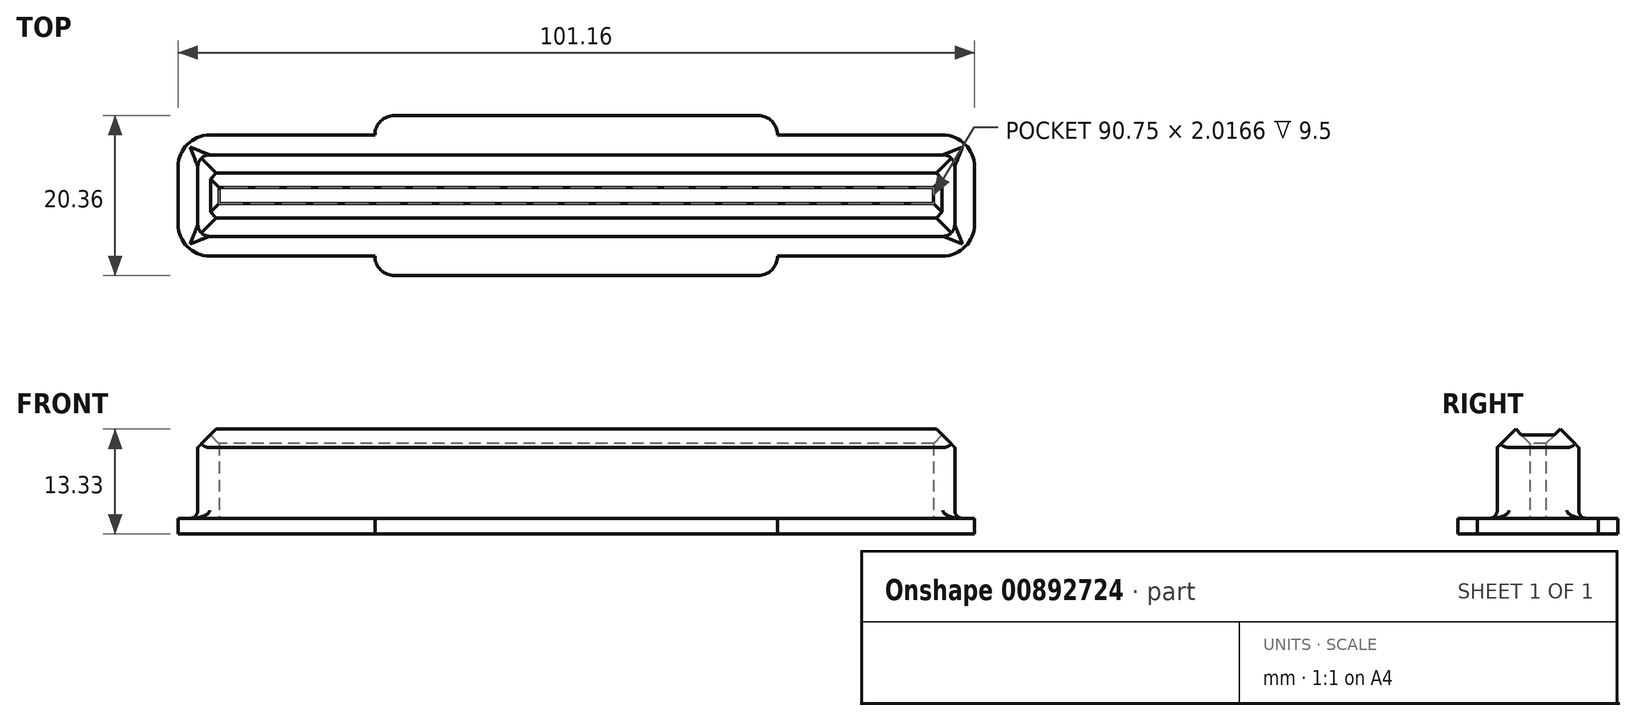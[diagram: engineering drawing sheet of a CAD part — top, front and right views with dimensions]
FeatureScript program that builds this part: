
annotation { "Feature Type Name" : "Feature", "Feature Type Description" : "" }
export const myFeature = defineFeature(function(context is Context, id is Id, definition is map)
    precondition{}
    {
        {
            var Q0;
            Q0=qCreatedBy(makeId("Top.planeOp"),FACE);
            var sketch = newSketch(context, id + "F0", { "sketchPlane" : qUnion([Q0])});
            skLineSegment(sketch, "E0.bottom", {"start": v(48.08, 5.18) * mm, "end": v(-48.08, 5.18) * mm});
            skLineSegment(sketch, "E0.top", {"start": v(48.08, -5.17) * mm, "end": v(-48.08, -5.17) * mm});
            skLineSegment(sketch, "E0.left", {"start": v(48.08, 5.17) * mm, "end": v(48.08, -5.18) * mm});
            skLineSegment(sketch, "E0.right", {"start": v(-48.08, 5.18) * mm, "end": v(-48.08, -5.17) * mm});
            skPoint(sketch, "E0.middle", {"position": v(0, 0) * mm});
            skLineSegment(sketch, "E1.bottom", {"start": v(-50.58, 7.68) * mm, "end": v(50.58, 7.68) * mm});
            skLineSegment(sketch, "E1.top", {"start": v(-50.58, -7.68) * mm, "end": v(50.58, -7.68) * mm});
            skLineSegment(sketch, "E1.left", {"start": v(-50.58, 7.68) * mm, "end": v(-50.58, -7.67) * mm});
            skLineSegment(sketch, "E1.right", {"start": v(50.58, 7.67) * mm, "end": v(50.58, -7.68) * mm});
            skLineSegment(sketch, "E2.bottom", {"start": v(-45.38, 1) * mm, "end": v(45.38, 1) * mm});
            skLineSegment(sketch, "E2.top", {"start": v(-45.38, -1) * mm, "end": v(45.38, -1) * mm});
            skLineSegment(sketch, "E2.left", {"start": v(-45.38, 1) * mm, "end": v(-45.38, -1) * mm});
            skLineSegment(sketch, "E2.right", {"start": v(45.38, 1) * mm, "end": v(45.38, -1) * mm});
            skLineSegment(sketch, "E3", {"start": v(-25.57, 7.67) * mm, "end": v(-25.57, 10.18) * mm});
            skLineSegment(sketch, "E4", {"start": v(-25.57, 10.18) * mm, "end": v(0, 10.18) * mm});
            skLineSegment(sketch, "E5.MirrorCS", {"start": v(25.57, 10.18) * mm, "end": v(0, 10.17) * mm});
            skLineSegment(sketch, "E6.MirrorCS", {"start": v(25.57, 7.67) * mm, "end": v(25.57, 10.18) * mm});
            skLineSegment(sketch, "E7.MirrorCS", {"start": v(-25.58, -7.67) * mm, "end": v(-25.58, -10.18) * mm});
            skLineSegment(sketch, "E8.MirrorCS", {"start": v(-25.57, -10.18) * mm, "end": v(0, -10.17) * mm});
            skLineSegment(sketch, "E9.MirrorCS", {"start": v(25.57, -10.18) * mm, "end": v(0, -10.18) * mm});
            skLineSegment(sketch, "E10.MirrorCS", {"start": v(25.57, -7.67) * mm, "end": v(25.57, -10.18) * mm});
            skSolve(sketch);
        }
        {
            var Q0;
            Q0=makeQuery(id+"F0.imprint","IMPRINT",FACE,{"disambiguationData":[TD([[makeQuery(id+"F0.imprint","IMPRINT",EDGE,{"derivedFrom":sQuery(id+"F0.wireOp",EDGE,"E0.bottom")}),-1.0]])]});
            var Q1;
            Q1=makeQuery(id+"F0.imprint","IMPRINT",FACE,{"disambiguationData":[TD([[makeQuery(id+"F0.imprint","IMPRINT",EDGE,{"derivedFrom":sQuery(id+"F0.wireOp",EDGE,"E0.bottom")}),1.0]])]});
            var Q2;
            Q2=makeQuery(id+"F0.imprint","IMPRINT",FACE,{"disambiguationData":[TD([[makeQuery(id+"F0.imprint","IMPRINT",EDGE,{"derivedFrom":sQuery(id+"F0.wireOp",EDGE,"E2.bottom")}),-1.0]])]});
            extrude(context, id + "F1", {"entities" : qUnion([Q0, Q1, Q2]), "oppositeDirection" : true, "depth" : 2 * mm, "offsetDistance" : 25 * mm});
        }
        {
            var Q0;
            Q0=makeQuery(id+"F0.imprint","IMPRINT",FACE,{"disambiguationData":[TD([[makeQuery(id+"F0.imprint","IMPRINT",EDGE,{"derivedFrom":sQuery(id+"F0.wireOp",EDGE,"E0.bottom")}),1.0]])]});
            extrude(context, id + "F2", {"entities" : qUnion([Q0]), "operationType" : NewBodyOperationType.ADD, "depth" : 11.5 * mm, "offsetDistance" : 25 * mm});
        }
        {
            var Q0;
            {var subQ0=sQuery(id+"F0.wireOp",EDGE,"E3");Q0=makeQuery(id+"F0.imprint","IMPRINT",FACE,{"disambiguationData":[TD([[makeQuery(id+"F0.imprint","IMPRINT",EDGE,{"derivedFrom":subQ0}),-1.0]])]});}
            var Q1;
            {var subQ0=sQuery(id+"F0.wireOp",EDGE,"E7.MirrorCS");Q1=makeQuery(id+"F0.imprint","IMPRINT",FACE,{"disambiguationData":[TD([[makeQuery(id+"F0.imprint","IMPRINT",EDGE,{"derivedFrom":subQ0}),1.0]])]});}
            extrude(context, id + "F3", {"entities" : qUnion([Q0, Q1]), "operationType" : NewBodyOperationType.ADD, "oppositeDirection" : true, "depth" : 2 * mm, "offsetDistance" : 25 * mm});
        }
        {
            var Q0;
            Q0=makeQuery(id+"F2.opExtrude","CAP_EDGE",EDGE,{"disambiguationData":[OSD([sQuery(id+"F0.wireOp",EDGE,"E0.top")])],"isStart":false});
            var Q1;
            Q1=makeQuery(id+"F2.opExtrude","CAP_EDGE",EDGE,{"disambiguationData":[OSD([sQuery(id+"F0.wireOp",EDGE,"E0.right")])],"isStart":false});
            var Q2;
            Q2=makeQuery(id+"F2.opExtrude","CAP_EDGE",EDGE,{"disambiguationData":[OSD([sQuery(id+"F0.wireOp",EDGE,"E0.bottom")])],"isStart":false});
            var Q3;
            Q3=makeQuery(id+"F2.opExtrude","CAP_EDGE",EDGE,{"disambiguationData":[OSD([sQuery(id+"F0.wireOp",EDGE,"E0.left")])],"isStart":false});
            chamfer(context, id + "F4", {"entities" : qUnion([Q0, Q1, Q2, Q3]), "width" : 2.5 * mm, "tangentPropagation" : true});
        }
        {
            var Q0;
            Q0=makeQuery(id+"F2.opExtrude","CAP_EDGE",EDGE,{"disambiguationData":[OSD([sQuery(id+"F0.wireOp",EDGE,"E2.bottom")])],"isStart":false});
            var Q1;
            Q1=makeQuery(id+"F2.opExtrude","CAP_EDGE",EDGE,{"disambiguationData":[OSD([sQuery(id+"F0.wireOp",EDGE,"E2.left")])],"isStart":false});
            var Q2;
            Q2=makeQuery(id+"F2.opExtrude","CAP_EDGE",EDGE,{"disambiguationData":[OSD([sQuery(id+"F0.wireOp",EDGE,"E2.top")])],"isStart":false});
            var Q3;
            Q3=makeQuery(id+"F2.opExtrude","CAP_EDGE",EDGE,{"disambiguationData":[OSD([sQuery(id+"F0.wireOp",EDGE,"E2.right")])],"isStart":false});
            chamfer(context, id + "F5", {"entities" : qUnion([Q0, Q1, Q2, Q3]), "width" : 2 * mm, "tangentPropagation" : true});
        }
        {
            var Q0;
            Q0=makeQuery(id+"F2.opExtrude","CAP_EDGE",EDGE,{"disambiguationData":[OSD([sQuery(id+"F0.wireOp",EDGE,"E0.top")])],"isStart":true});
            var Q1;
            Q1=makeQuery(id+"F2.opExtrude","CAP_EDGE",EDGE,{"disambiguationData":[OSD([sQuery(id+"F0.wireOp",EDGE,"E0.right")])],"isStart":true});
            var Q2;
            Q2=makeQuery(id+"F2.opExtrude","CAP_EDGE",EDGE,{"disambiguationData":[OSD([sQuery(id+"F0.wireOp",EDGE,"E0.bottom")])],"isStart":true});
            var Q3;
            Q3=makeQuery(id+"F2.opExtrude","CAP_EDGE",EDGE,{"disambiguationData":[OSD([sQuery(id+"F0.wireOp",EDGE,"E0.left")])],"isStart":true});
            fillet(context, id + "F6", {"entities" : qUnion([Q0, Q1, Q2, Q3]), "radius" : 1 * mm, "tangentPropagation" : true, "allowEdgeOverflow" : false});
        }
        {
            var Q0;
            Q0=makeQuery(id+"F2.opExtrude","SWEPT_EDGE",EDGE,{"disambiguationData":[OSD([sQuery(id+"F0.wireOp",EDGE,"E0.bottom"),sQuery(id+"F0.wireOp",EDGE,"E0.right")])]});
            var Q1;
            Q1=makeQuery(id+"F2.opExtrude","SWEPT_EDGE",EDGE,{"disambiguationData":[OSD([sQuery(id+"F0.wireOp",EDGE,"E0.top"),sQuery(id+"F0.wireOp",EDGE,"E0.right")])]});
            var Q2;
            Q2=makeQuery(id+"F2.opExtrude","SWEPT_EDGE",EDGE,{"disambiguationData":[OSD([sQuery(id+"F0.wireOp",EDGE,"E0.top"),sQuery(id+"F0.wireOp",EDGE,"E0.left")])]});
            var Q3;
            Q3=makeQuery(id+"F2.opExtrude","SWEPT_EDGE",EDGE,{"disambiguationData":[OSD([sQuery(id+"F0.wireOp",EDGE,"E0.bottom"),sQuery(id+"F0.wireOp",EDGE,"E0.left")])]});
            fillet(context, id + "F7", {"entities" : qUnion([Q0, Q1, Q2, Q3]), "radius" : 1.5 * mm, "tangentPropagation" : true, "allowEdgeOverflow" : false});
        }
        {
            var Q0;
            Q0=makeQuery(id+"F3.opExtrude","SWEPT_EDGE",EDGE,{"disambiguationData":[OSD([sQuery(id+"F0.wireOp",EDGE,"E3"),sQuery(id+"F0.wireOp",EDGE,"E4")])]});
            var Q1;
            Q1=makeQuery(id+"F3.opExtrude","SWEPT_EDGE",EDGE,{"disambiguationData":[OSD([sQuery(id+"F0.wireOp",EDGE,"E5.MirrorCS"),sQuery(id+"F0.wireOp",EDGE,"E6.MirrorCS")])]});
            var Q2;
            Q2=makeQuery(id+"F3.opExtrude","SWEPT_EDGE",EDGE,{"disambiguationData":[OSD([sQuery(id+"F0.wireOp",EDGE,"E9.MirrorCS"),sQuery(id+"F0.wireOp",EDGE,"E10.MirrorCS")])]});
            var Q3;
            Q3=makeQuery(id+"F3.opExtrude","SWEPT_EDGE",EDGE,{"disambiguationData":[OSD([sQuery(id+"F0.wireOp",EDGE,"E7.MirrorCS"),sQuery(id+"F0.wireOp",EDGE,"E8.MirrorCS")])]});
            fillet(context, id + "F8", {"entities" : qUnion([Q0, Q1, Q2, Q3]), "radius" : 2.5 * mm, "tangentPropagation" : true, "allowEdgeOverflow" : false});
        }
        {
            var Q0;
            Q0=makeQuery(id+"F1.opExtrude","SWEPT_EDGE",EDGE,{"disambiguationData":[OSD([sQuery(id+"F0.wireOp",EDGE,"E1.bottom"),sQuery(id+"F0.wireOp",EDGE,"E1.left")])]});
            var Q1;
            Q1=makeQuery(id+"F1.opExtrude","SWEPT_EDGE",EDGE,{"disambiguationData":[OSD([sQuery(id+"F0.wireOp",EDGE,"E1.top"),sQuery(id+"F0.wireOp",EDGE,"E1.left")])]});
            var Q2;
            Q2=makeQuery(id+"F1.opExtrude","SWEPT_EDGE",EDGE,{"disambiguationData":[OSD([sQuery(id+"F0.wireOp",EDGE,"E1.top"),sQuery(id+"F0.wireOp",EDGE,"E1.right")])]});
            var Q3;
            Q3=makeQuery(id+"F1.opExtrude","SWEPT_EDGE",EDGE,{"disambiguationData":[OSD([sQuery(id+"F0.wireOp",EDGE,"E1.bottom"),sQuery(id+"F0.wireOp",EDGE,"E1.right")])]});
            fillet(context, id + "F9", {"entities" : qUnion([Q0, Q1, Q2, Q3]), "radius" : 4 * mm, "tangentPropagation" : true, "allowEdgeOverflow" : false});
        }
    });
